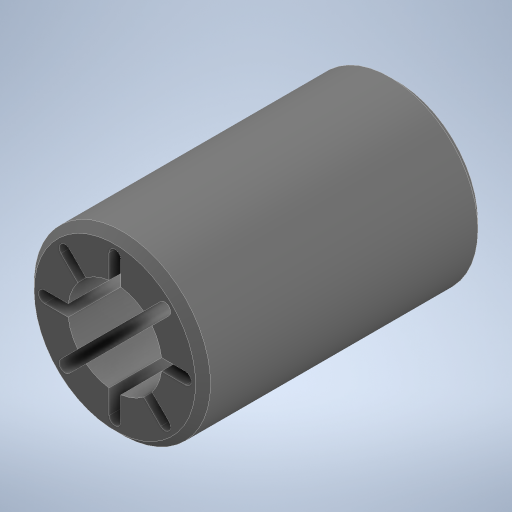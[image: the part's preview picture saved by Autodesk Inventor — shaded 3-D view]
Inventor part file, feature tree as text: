
AUTODESK INVENTOR PART (.ipt)
format: ipt  version: 2023 (Build 270158000, 158)  size: 272,384 bytes
history: native  units: in
note: dims shown in document units (in); Inventor stores cm internally (conversion verified against a paired STEP export)
features: extrude x2, sketch x2, chamfer x1
ambient origin geometry x8: Origin, YZ Plane, XZ Plane, XY Plane, X Axis, Y Axis, Z Axis, Center Point
bodies: Solid1 (feature_tree)
feature tree (5):
  extrude  "Extrusion1"  Depth=0.315in
  extrude  "Extrusion2"  Depth=0.0394in
  chamfer  "Chamfer1"  Distance=3.1496in Angle=360.0deg
  sketch  "Sketch1"  dims[d0=0.5906in d1=0.315in]
  sketch  "Sketch2"  dims[d2=0.9449in d3=0.0in d4=0.0394in d5=3.1496in d7=360.0deg d9=0.9449in d10=0.0in d11=0.025in d12=0.125in d13=45.0deg]
